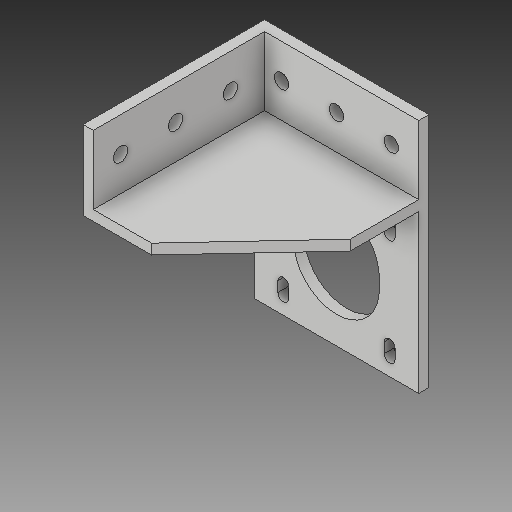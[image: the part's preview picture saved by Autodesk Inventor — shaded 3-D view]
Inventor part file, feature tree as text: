
AUTODESK INVENTOR PART (.ipt)
format: ipt  version: 2018 (Build 220112000, 112)  size: 187,904 bytes
history: native  units: in
note: dims shown in document units (in); Inventor stores cm internally (conversion verified against a paired STEP export)
features: sketch x8, other x3
ambient origin geometry x8: Origin, YZ Plane, XZ Plane, XY Plane, X Axis, Y Axis, Z Axis, Center Point
bodies: Solid1 (feature_tree)
feature tree (11):
  other  "MotorMount1.ipt"
  other  "Solid1::MotorMount1.ipt"
  other  "TaggingFeature1"
  sketch  "Sketch1"  dims[d0=0.3937in]
  sketch  "Sketch2"
  sketch  "Sketch3"
  sketch  "Sketch4"
  sketch  "Sketch8"
  sketch  "Sketch9"
  sketch  "Sketch10"
  sketch  "Sketch11"
